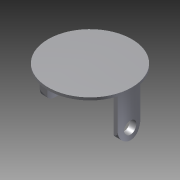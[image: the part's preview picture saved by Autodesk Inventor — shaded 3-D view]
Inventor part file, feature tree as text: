
AUTODESK INVENTOR PART (.ipt)
format: ipt  version: 2014 (Build 180170000, 170)  size: 130,048 bytes
history: native  units: in
note: dims shown in document units (in); Inventor stores cm internally (conversion verified against a paired STEP export)
features: other x7, extrude x5, sketch x5
ambient origin geometry x8: Origin, YZ Plane, XZ Plane, XY Plane, X Axis, Y Axis, Z Axis, Center Point
bodies: Solid1 (feature_tree)
feature tree (17):
  extrude  "Extrusion1"  Depth=0.167in TaperAngle=0.0deg
  extrude  "Extrusion2"  Depth=0.644in TaperAngle=0.0deg
  extrude  "Extrusion3"  [1 undecoded]
  extrude  "Extrusion4"  [1 undecoded]
  extrude  "Extrusion5"  [1 undecoded]
  other  "to_trmnl_hold_XY"
  other  "to_trmnl_hold_YZ"
  other  "to_trmnl_hold_ZX"
  other  "to_trmnl_hold_X"
  other  "to_trmnl_hold_Y"
  other  "to_trmnl_hold_Z"
  other  "to_trmnl_hold_Center"
  sketch  "Sketch_2"  dims[d0=0.01in d1=0.0in d2=0.167in d3=0.0in]
  sketch  "Sketch_3"  dims[d4=0.167in d5=0.0in d6=0.644in d7=0.0in]
  sketch  "Sketch_4"  dims[d8=0.644in d9=0.0in]
  sketch  "Sketch_5"
  sketch  "Sketch_6"
note: 3 required parameter values undecoded (feature->parameter linkage not recoverable at this tier; creation-order binding heuristic only, values carry confidence <= 0.55)
